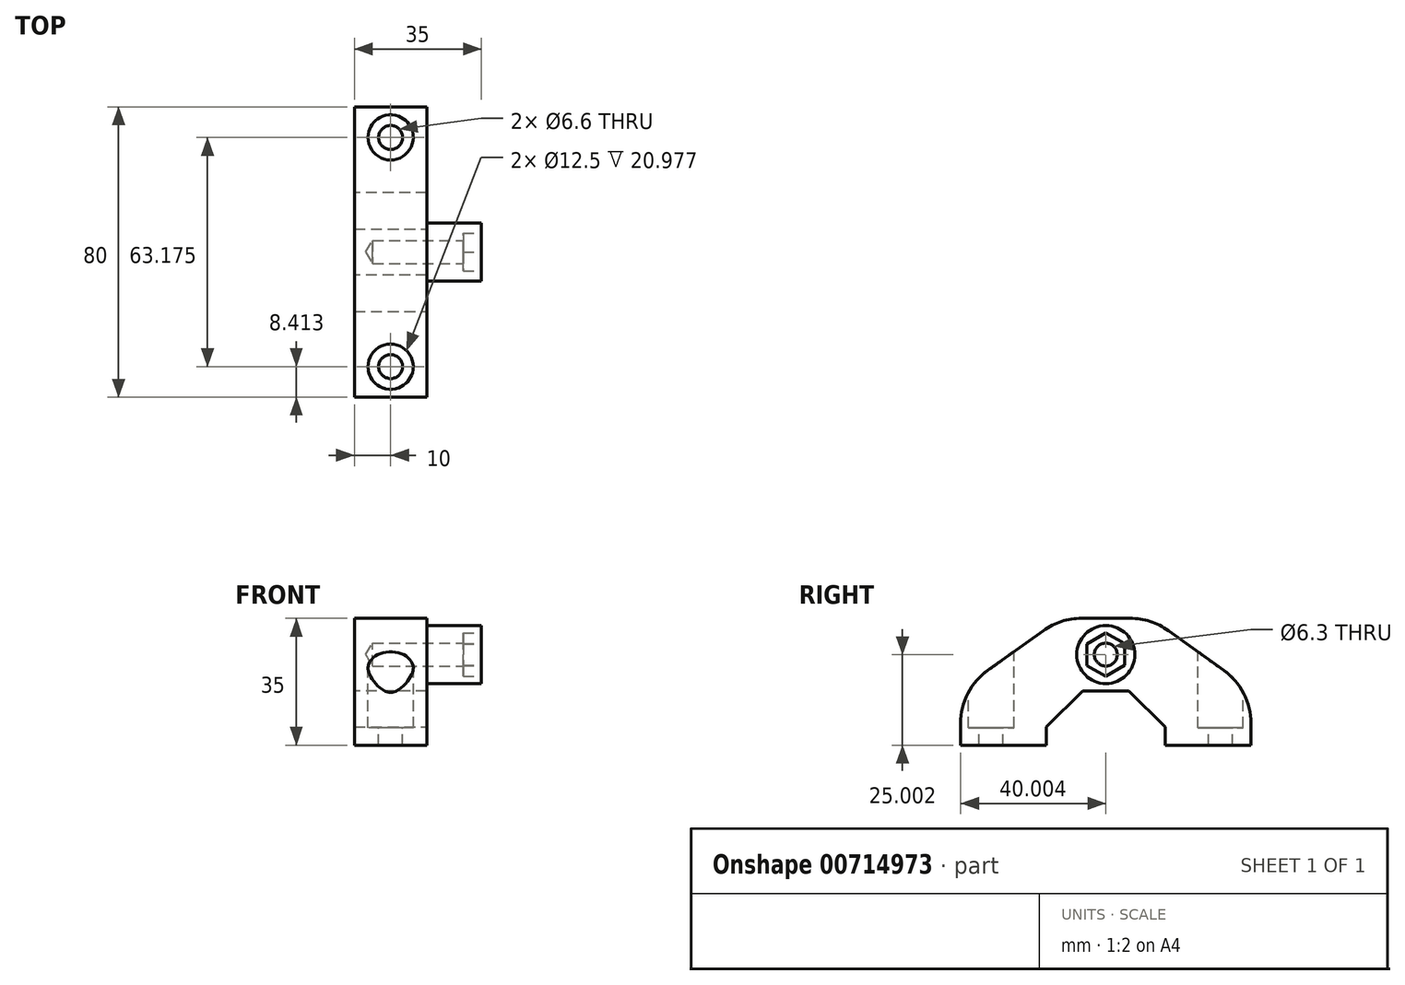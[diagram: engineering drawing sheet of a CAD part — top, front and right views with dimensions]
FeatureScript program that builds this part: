
annotation { "Feature Type Name" : "Feature", "Feature Type Description" : "" }
export const myFeature = defineFeature(function(context is Context, id is Id, definition is map)
    precondition{}
    {
        {
            var Q0;
            Q0=qCreatedBy(makeId("Right.planeOp"),FACE);
            var sketch = newSketch(context, id + "F0", { "sketchPlane" : qUnion([Q0])});
            skLineSegment(sketch, "E0", {"start": v(-16.38, 10) * mm, "end": v(-16.38, 0) * mm});
            skLineSegment(sketch, "E1", {"start": v(-40, 15.3) * mm, "end": v(-40, 0) * mm});
            skLineSegment(sketch, "E2", {"start": v(-40, 15.3) * mm, "end": v(-12.5, 35) * mm});
            skLineSegment(sketch, "E3", {"start": v(-40, 0) * mm, "end": v(-16.38, 0) * mm});
            skLineSegment(sketch, "E4", {"start": v(-12.5, 35) * mm, "end": v(0, 35) * mm});
            skLineSegment(sketch, "E5.MirrorCS", {"start": v(12.5, 35) * mm, "end": v(0, 35) * mm});
            skLineSegment(sketch, "E6.MirrorCS", {"start": v(40, 15.3) * mm, "end": v(40, 0) * mm});
            skLineSegment(sketch, "E7.MirrorCS", {"start": v(16.38, 10) * mm, "end": v(16.38, 0) * mm});
            skLineSegment(sketch, "E8.MirrorCS", {"start": v(40, 0) * mm, "end": v(16.38, 0) * mm});
            skLineSegment(sketch, "E9.MirrorCS", {"start": v(40, 15.3) * mm, "end": v(12.5, 35) * mm});
            skLineSegment(sketch, "E10", {"start": v(-16.38, 10) * mm, "end": v(-16.38, 15) * mm});
            skLineSegment(sketch, "E11", {"start": v(16.38, 10) * mm, "end": v(16.38, 15) * mm});
            skLineSegment(sketch, "E12", {"start": v(-16.38, 15) * mm, "end": v(16.38, 15) * mm});
            skSolve(sketch);
        }
        {
            var Q0;
            Q0=makeQuery(id+"F0.imprint","IMPRINT",FACE,{"disambiguationData":[TD([[makeQuery(id+"F0.imprint","IMPRINT",EDGE,{"derivedFrom":sQuery(id+"F0.wireOp",EDGE,"E0")}),-1.0]])]});
            extrude(context, id + "F1", {"entities" : qUnion([Q0]), "oppositeDirection" : true, "depth" : 20 * mm, "offsetDistance" : 25 * mm});
        }
        {
            var Q0;
            Q0=makeQuery(id+"F1.opExtrude","CAP_FACE",FACE,{"disambiguationData":[OSD([sQuery(id+"F0.wireOp",EDGE,"C0jItkj8-S1HE-fXET-6T7l-2sPWsG6ps4In"),sQuery(id+"F0.wireOp",EDGE,"ztHHr7Qy-1UEx-xfbj-iBV5-9dU8PU1vMr4F"),sQuery(id+"F0.wireOp",EDGE,"E0"),sQuery(id+"F0.wireOp",EDGE,"E1"),sQuery(id+"F0.wireOp",EDGE,"E2"),sQuery(id+"F0.wireOp",EDGE,"E3"),sQuery(id+"F0.wireOp",EDGE,"Bf5PFNSV-KWP0-icE1-BQTD-RrxF0XhyywQw"),sQuery(id+"F0.wireOp",EDGE,"E4"),sQuery(id+"F0.wireOp",EDGE,"668fd534-b627-440b-b2d7-282948e1eaf00.MirrorCS"),sQuery(id+"F0.wireOp",EDGE,"E5.MirrorCS"),sQuery(id+"F0.wireOp",EDGE,"668fd534-b627-440b-b2d7-282948e1eaf03.MirrorCS"),sQuery(id+"F0.wireOp",EDGE,"E6.MirrorCS"),sQuery(id+"F0.wireOp",EDGE,"E7.MirrorCS"),sQuery(id+"F0.wireOp",EDGE,"E8.MirrorCS"),sQuery(id+"F0.wireOp",EDGE,"668fd534-b627-440b-b2d7-282948e1eaf07.MirrorCS"),sQuery(id+"F0.wireOp",EDGE,"E9.MirrorCS")])],"isStart":true});
            var sketch = newSketch(context, id + "F2", { "sketchPlane" : qUnion([Q0])});
            skPoint(sketch, "E13", {"position": v(0, 25) * mm});
            skCircle(sketch, "E14", {"center": v(0, 25) * mm, "radius": 8 * mm});
            skLineSegment(sketch, "E15", {"start": v(0, 15) * mm, "end": v(0, 35) * mm});
            skSolve(sketch);
        }
        {
            var Q0;
            Q0 = qSketchRegion(id + "F2", true);
            extrude(context, id + "F3", {"entities" : qUnion([Q0]), "operationType" : NewBodyOperationType.ADD, "depth" : 15 * mm, "offsetDistance" : 25 * mm});
        }
        {
            var Q0;
            Q0=makeQuery(id+"F3.opExtrude","CAP_FACE",FACE,{"disambiguationData":[OSD([sQuery(id+"F2.wireOp",EDGE,"E14")])],"isStart":false});
            var sketch = newSketch(context, id + "F4", { "sketchPlane" : qUnion([Q0])});
            skPoint(sketch, "E16", {"position": v(0, 25) * mm});
            skCircle(sketch, "E17.cCircle", {"center": v(0, 25) * mm, "radius": 5.2 * mm, "construction": true});
            skLineSegment(sketch, "E17.0", {"start": v(-0.04, 31) * mm, "end": v(5.18, 28.04) * mm});
            skLineSegment(sketch, "E17.1", {"start": v(5.18, 28.04) * mm, "end": v(5.22, 22.04) * mm});
            skLineSegment(sketch, "E17.2", {"start": v(5.22, 22.04) * mm, "end": v(0.05, 19) * mm});
            skLineSegment(sketch, "E17.3", {"start": v(0.05, 19) * mm, "end": v(-5.18, 21.96) * mm});
            skLineSegment(sketch, "E17.4", {"start": v(-5.18, 21.96) * mm, "end": v(-5.22, 27.97) * mm});
            skLineSegment(sketch, "E17.5", {"start": v(-5.22, 27.97) * mm, "end": v(-0.04, 31) * mm});
            skPoint(sketch, "E17.0.midPoint", {"position": v(2.57, 29.52) * mm});
            skSolve(sketch);
        }
        {
            var Q0;
            Q0=sQuery(id+"F4.wireOp",VERTEX,"E16");
            var Q1;
            Q1=makeQuery(id+"F1.opExtrude","SWEPT_BODY",BODY,{"disambiguationData":[OSD([sQuery(id+"F0.wireOp",EDGE,"C0jItkj8-S1HE-fXET-6T7l-2sPWsG6ps4In"),sQuery(id+"F0.wireOp",EDGE,"ztHHr7Qy-1UEx-xfbj-iBV5-9dU8PU1vMr4F"),sQuery(id+"F0.wireOp",EDGE,"E0"),sQuery(id+"F0.wireOp",EDGE,"E1"),sQuery(id+"F0.wireOp",EDGE,"E2"),sQuery(id+"F0.wireOp",EDGE,"E3"),sQuery(id+"F0.wireOp",EDGE,"Bf5PFNSV-KWP0-icE1-BQTD-RrxF0XhyywQw"),sQuery(id+"F0.wireOp",EDGE,"E4"),sQuery(id+"F0.wireOp",EDGE,"668fd534-b627-440b-b2d7-282948e1eaf00.MirrorCS"),sQuery(id+"F0.wireOp",EDGE,"E5.MirrorCS"),sQuery(id+"F0.wireOp",EDGE,"668fd534-b627-440b-b2d7-282948e1eaf03.MirrorCS"),sQuery(id+"F0.wireOp",EDGE,"E6.MirrorCS"),sQuery(id+"F0.wireOp",EDGE,"E7.MirrorCS"),sQuery(id+"F0.wireOp",EDGE,"E8.MirrorCS"),sQuery(id+"F0.wireOp",EDGE,"668fd534-b627-440b-b2d7-282948e1eaf07.MirrorCS"),sQuery(id+"F0.wireOp",EDGE,"E9.MirrorCS")])]});
            hole(context, id + "F5", {"style" : HoleStyle.SIMPLE, "endStyle" : HoleEndStyle.BLIND, "standardTappedOrClearance" : lookupTablePath({ "standard" : "ISO", "fit" : "Close", "size" : "M6", "type" : "Clearance" }), "standardBlindInLast" : lookupTablePath({ "fit" : "Close", "standard" : "ISO", "size" : "M6", "type" : "Clearance" }), "holeDiameter" : 6.3 * mm, "majorDiameter" : 5 * mm, "holeDepth" : 30 * mm, "isTappedThrough" : true, "tappedDepth" : 12 * mm, "tapClearance" : 3, "locations" : qUnion([Q0]), "scope" : qUnion([Q1])});
        }
        {
            var Q0;
            Q0 = qSketchRegion(id + "F4", true);
            extrude(context, id + "F6", {"entities" : qUnion([Q0]), "operationType" : NewBodyOperationType.REMOVE, "oppositeDirection" : true, "depth" : 5 * mm, "offsetDistance" : 25 * mm});
        }
        {
            var Q0;
            Q0=makeQuery(id+"F1.opExtrude","SWEPT_FACE",FACE,{"disambiguationData":[OSD([sQuery(id+"F0.wireOp",EDGE,"E4"),sQuery(id+"F0.wireOp",EDGE,"E5.MirrorCS")])]});
            var sketch = newSketch(context, id + "F7", { "sketchPlane" : qUnion([Q0])});
            skLineSegment(sketch, "E18", {"start": v(-20, 39.98) * mm, "end": v(0, 39.98) * mm});
            skLineSegment(sketch, "E19", {"start": v(-10, 39.98) * mm, "end": v(-10, 23.2) * mm});
            skPoint(sketch, "E20", {"position": v(-10, 31.59) * mm});
            skPoint(sketch, "E21.MirrorP", {"position": v(-10, -31.59) * mm});
            skLineSegment(sketch, "E22.MirrorCS", {"start": v(-10, -39.98) * mm, "end": v(-10, -23.2) * mm});
            skLineSegment(sketch, "E23.MirrorCS", {"start": v(-20, -39.98) * mm, "end": v(0, -39.98) * mm});
            skSolve(sketch);
        }
        {
            var Q0;
            Q0=sQuery(id+"F7.wireOp",VERTEX,"E20");
            var Q1;
            Q1=sQuery(id+"F7.wireOp",VERTEX,"E21.MirrorP");
            var Q2;
            Q2=makeQuery(id+"F1.opExtrude","SWEPT_BODY",BODY,{"disambiguationData":[OSD([sQuery(id+"F0.wireOp",EDGE,"C0jItkj8-S1HE-fXET-6T7l-2sPWsG6ps4In"),sQuery(id+"F0.wireOp",EDGE,"ztHHr7Qy-1UEx-xfbj-iBV5-9dU8PU1vMr4F"),sQuery(id+"F0.wireOp",EDGE,"E0"),sQuery(id+"F0.wireOp",EDGE,"E1"),sQuery(id+"F0.wireOp",EDGE,"E2"),sQuery(id+"F0.wireOp",EDGE,"E3"),sQuery(id+"F0.wireOp",EDGE,"Bf5PFNSV-KWP0-icE1-BQTD-RrxF0XhyywQw"),sQuery(id+"F0.wireOp",EDGE,"E4"),sQuery(id+"F0.wireOp",EDGE,"668fd534-b627-440b-b2d7-282948e1eaf00.MirrorCS"),sQuery(id+"F0.wireOp",EDGE,"E5.MirrorCS"),sQuery(id+"F0.wireOp",EDGE,"668fd534-b627-440b-b2d7-282948e1eaf03.MirrorCS"),sQuery(id+"F0.wireOp",EDGE,"E6.MirrorCS"),sQuery(id+"F0.wireOp",EDGE,"E7.MirrorCS"),sQuery(id+"F0.wireOp",EDGE,"E8.MirrorCS"),sQuery(id+"F0.wireOp",EDGE,"668fd534-b627-440b-b2d7-282948e1eaf07.MirrorCS"),sQuery(id+"F0.wireOp",EDGE,"E9.MirrorCS")])]});
            hole(context, id + "F8", {"style" : HoleStyle.C_BORE, "endStyle" : HoleEndStyle.BLIND, "holeDiameter" : 6.6 * mm, "cBoreDiameter" : 12.5 * mm, "cBoreDepth" : 12 * mm, "majorDiameter" : 5 * mm, "holeDepth" : 21 * mm, "isTappedThrough" : true, "tappedDepth" : 12 * mm, "tapClearance" : 3, "locations" : qUnion([Q0, Q1]), "scope" : qUnion([Q2])});
        }
        {
            var Q0;
            Q0=makeQuery(id+"F1.opExtrude","SWEPT_EDGE",EDGE,{"disambiguationData":[OSD([sQuery(id+"F0.wireOp",EDGE,"E6.MirrorCS"),sQuery(id+"F0.wireOp",EDGE,"E9.MirrorCS")])]});
            var Q1;
            Q1=makeQuery(id+"F1.opExtrude","SWEPT_EDGE",EDGE,{"disambiguationData":[OSD([sQuery(id+"F0.wireOp",EDGE,"E5.MirrorCS"),sQuery(id+"F0.wireOp",EDGE,"E9.MirrorCS")])]});
            var Q2;
            Q2=makeQuery(id+"F1.opExtrude","SWEPT_EDGE",EDGE,{"disambiguationData":[OSD([sQuery(id+"F0.wireOp",EDGE,"E2"),sQuery(id+"F0.wireOp",EDGE,"E4")])]});
            var Q3;
            Q3=makeQuery(id+"F1.opExtrude","SWEPT_EDGE",EDGE,{"disambiguationData":[OSD([sQuery(id+"F0.wireOp",EDGE,"E1"),sQuery(id+"F0.wireOp",EDGE,"E2")])]});
            fillet(context, id + "F9", {"entities" : qUnion([Q0, Q1, Q2, Q3]), "radius" : 18 * mm, "tangentPropagation" : true, "allowEdgeOverflow" : false});
        }
        {
            var Q0;
            Q0=makeQuery(id+"F1.opExtrude","SWEPT_EDGE",EDGE,{"disambiguationData":[OSD([sQuery(id+"F0.wireOp",EDGE,"E11"),sQuery(id+"F0.wireOp",EDGE,"E12")])]});
            var Q1;
            Q1=makeQuery(id+"F1.opExtrude","SWEPT_EDGE",EDGE,{"disambiguationData":[OSD([sQuery(id+"F0.wireOp",EDGE,"E10"),sQuery(id+"F0.wireOp",EDGE,"E12")])]});
            chamfer(context, id + "F10", {"entities" : qUnion([Q0, Q1]), "width" : 10 * mm, "tangentPropagation" : true});
        }
    });
